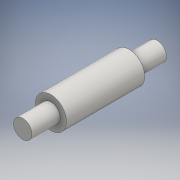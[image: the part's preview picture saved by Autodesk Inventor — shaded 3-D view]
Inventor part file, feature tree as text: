
AUTODESK INVENTOR PART (.ipt)
format: ipt  version: 2016 (Build 200138000, 138)  size: 107,520 bytes
history: native  units: mm
features: extrude x3, sketch x3
ambient origin geometry x8: Origin, YZ Plane, XZ Plane, XY Plane, X Axis, Y Axis, Z Axis, Center Point
bodies: Solid1 (feature_tree)
feature tree (6):
  extrude  "Extrusion1"  Depth=9.0mm TaperAngle=0.0deg
  extrude  "Extrusion2"  Depth=25.0mm TaperAngle=0.0deg
  extrude  "Extrusion3"  Depth=9.0mm
  sketch  "Sketch1"  dims[d0=5.9mm d1=9.0mm d2=0.0mm]
  sketch  "Sketch2"  dims[d3=10.0mm d4=25.0mm d5=0.0mm]
  sketch  "Sketch3"  dims[d6=6.0mm d7=5.9mm d8=9.0mm d9=0.0mm]
